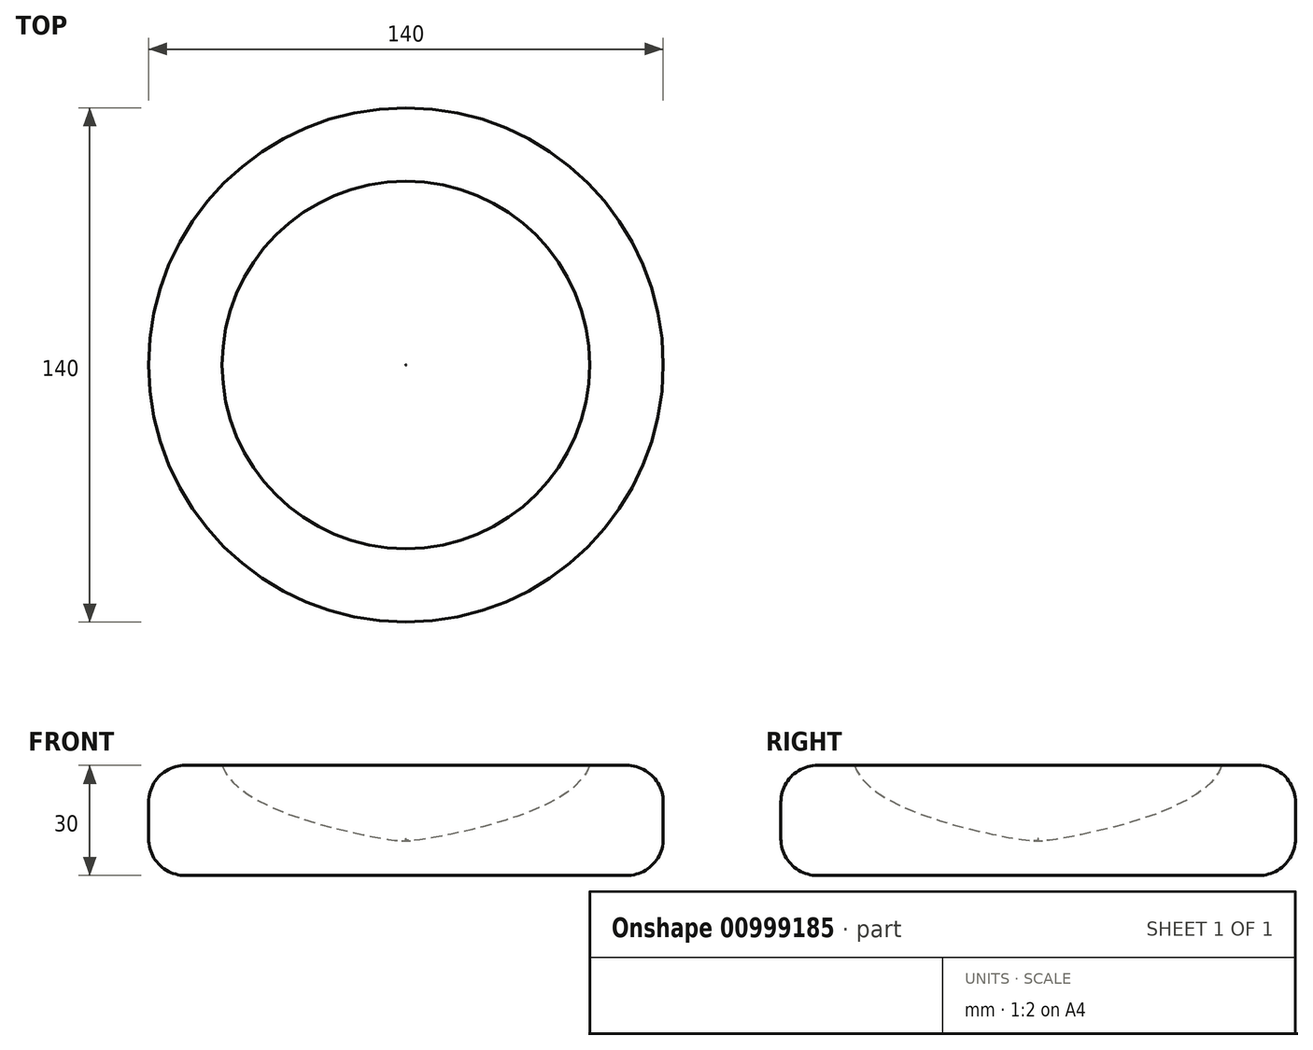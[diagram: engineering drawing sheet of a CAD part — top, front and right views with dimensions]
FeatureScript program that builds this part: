
annotation { "Feature Type Name" : "Feature", "Feature Type Description" : "" }
export const myFeature = defineFeature(function(context is Context, id is Id, definition is map)
    precondition{}
    {
        {
            var Q0;
            Q0=qCreatedBy(makeId("Front.planeOp"),FACE);
            var sketch = newSketch(context, id + "F0", { "sketchPlane" : qUnion([Q0])});
            skLineSegment(sketch, "E0.bottom", {"start": v(-20.49, 9.34) * mm, "end": v(39.51, 9.34) * mm});
            skLineSegment(sketch, "E0.top", {"start": v(-20.49, -20.66) * mm, "end": v(39.51, -20.66) * mm});
            skLineSegment(sketch, "E0.left", {"start": v(-20.49, -10.58) * mm, "end": v(-20.49, -20.66) * mm});
            skLineSegment(sketch, "E0.right", {"start": v(49.51, -0.66) * mm, "end": v(49.51, -10.66) * mm});
            skPoint(sketch, "E1.visualSharp", {"position": v(49.51, -20.66) * mm});
            skArc(sketch, "E1.filletArc", {"start": v(39.51, -20.66) * mm, "mid": v(46.58, -17.74) * mm, "end": v(49.51, -10.66) * mm});
            skPoint(sketch, "E2.visualSharp", {"position": v(49.51, 9.34) * mm});
            skArc(sketch, "E2.filletArc", {"start": v(49.51, -0.66) * mm, "mid": v(46.58, 6.4) * mm, "end": v(39.51, 9.34) * mm});
            skFitSpline(sketch, "E3", {"points": [v(29.51, 9.34) * mm, v(-7.2, -9.2) * mm, v(-20.49, -10.92) * mm, v(-20.49, -10.58) * mm], "startDerivative": vector(-17.34, -50.23) * mm, "endDerivative": vector(2, 4.84) * mm});
            skSolve(sketch);
        }
        {
            var Q0;
            Q0 = qSketchRegion(id + "F0", true);
            var Q1;
            Q1=sQuery(id+"F0.wireOp",EDGE,"E0.left");
            revolve(context, id + "F1", {"surfaceOperationType" : NewSurfaceOperationType.NEW, "entities" : qUnion([Q0]), "axis" : qUnion([Q1]), "revolveType" : RevolveType.FULL});
        }
    });
